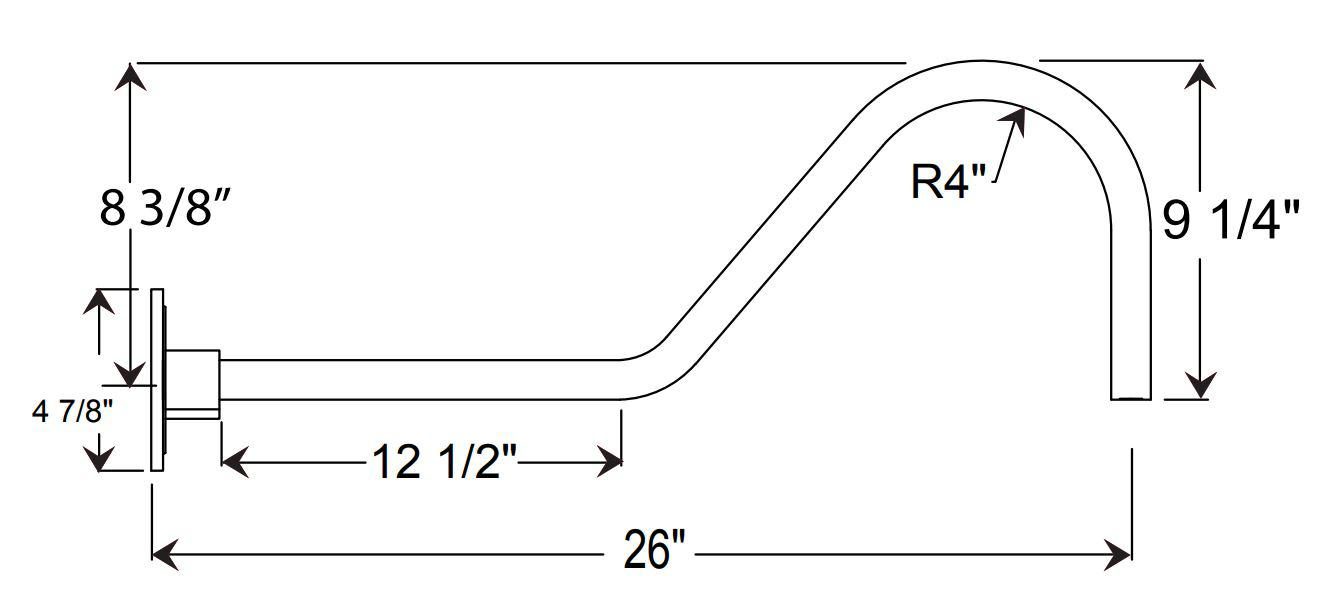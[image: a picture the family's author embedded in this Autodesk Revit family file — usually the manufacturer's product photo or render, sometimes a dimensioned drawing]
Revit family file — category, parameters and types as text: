
# Revit family: MILKCAN FT(8,10,12,18) MB
name_source: partatom
category: Lighting Fixtures
units: mm (PartAtom-declared; Revit-internal decimal feet)

## family parameters
Always vertical = Yes
Cut with Voids When Loaded = No
Light Source = Yes
OmniClass Number = 23.80.70.00
OmniClass Title = Lighting
Part Type = Normal
Room Calculation Point = No
Round Connector Dimension = Use Diameter
Shared = No
Work Plane-Based = No

## types (4) — shared parameters
Body Colour = Spun aluminium
Body Material = body
CRI = >90
Color Filter = 16777215
Construction Material = Heavy Duty spun aluminum.
Default Elevation = 0' - 0"
Description = 120-277 Voltage
Dimming = 1%
Dimming Lamp Color Temperature Shift = <None>
Efficiency = 65-125 lumens per watt
Life = L70 50,000 hours
Load Classification = Lighting
Manufacturer = ANP Lighting
Photometric Web File = generic.ies
Power Factor = 1
Tilt Angle = 90.00°
URL = https://www.anplighting.com
Voltage = 277 V
Warranty = 5 year limited warranty

## per-type parameters (varying)
| type | Apparent Load | Fixture Diameter | Fixture Height | Lamp | MCFT08 | MCFT10 | MCFT12 | MCFT18 | Wattage Comments | Weight |
| MCFT08 | 100 VA | 0' - 8" | 0' - 5" | MB | Yes | No | No | No | 100W Max | 1 lbs |
| MCFT10 | 100 VA | 0' - 10" | 0' - 5 1/2" | MB | No | Yes | No | No | 100W Max | 1 lbs |
| MCFT12 | 200 VA | 1' - 0" | 0' - 7" | LED | No | No | Yes | No | 200W Max | 1.5 lbs |
| MCFT18 | 200 VA | 1' - 6" | 0' - 8 1/2" | MB | No | No | No | Yes | 200W Max | 2.0 lbs |

note: column(s) folded — value = type name in every type: Model

## geometry (parser evidence)
native form markers: Sweep x34
no freeform markers — native parametric forms only
